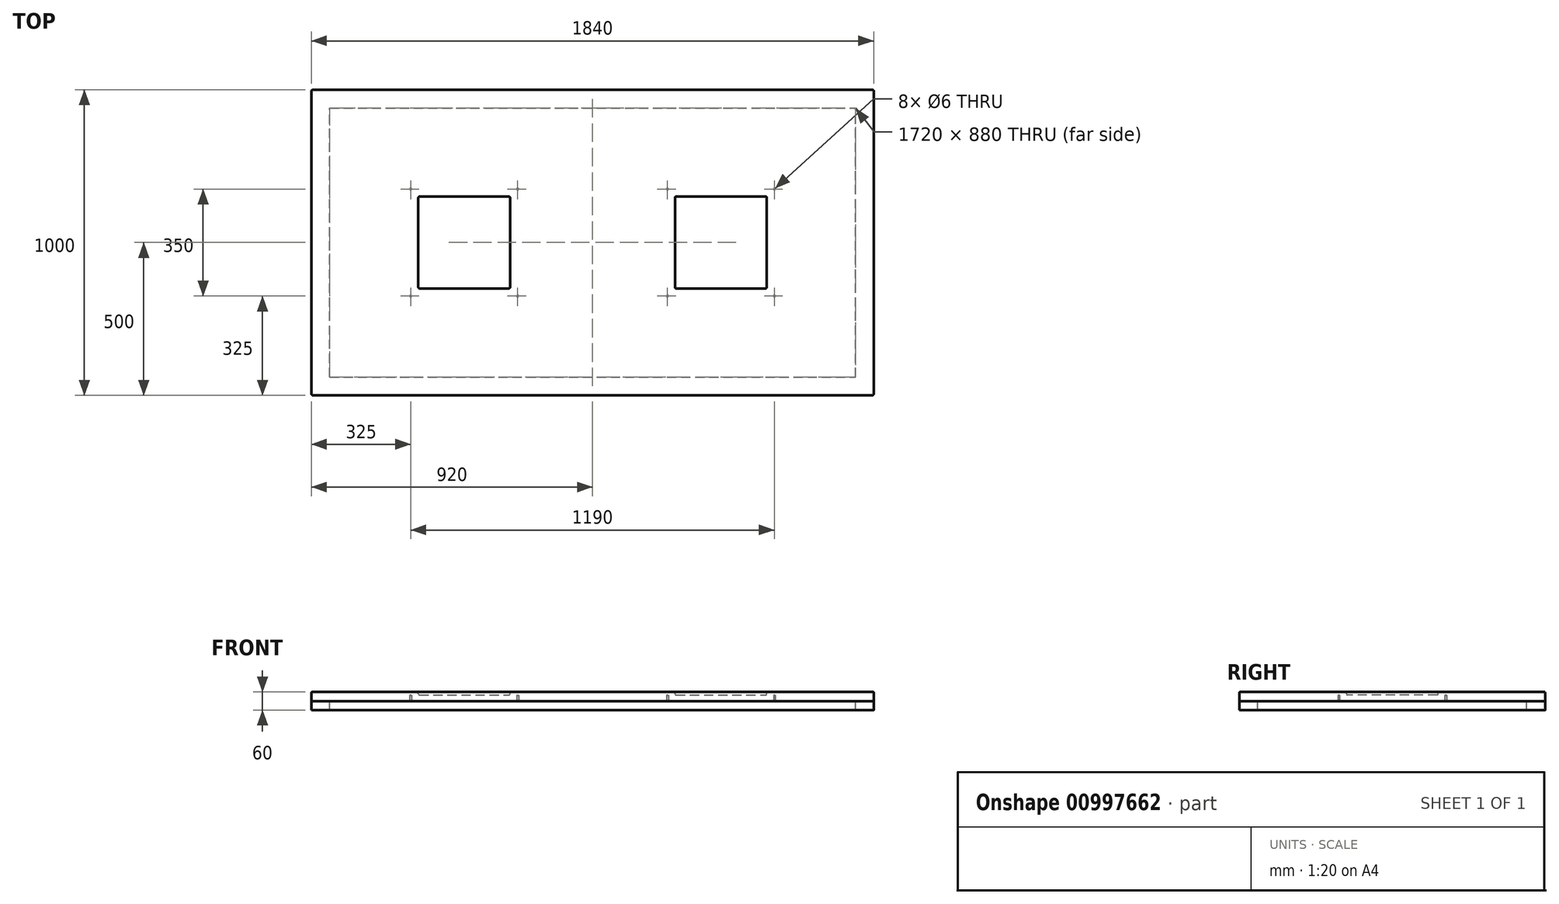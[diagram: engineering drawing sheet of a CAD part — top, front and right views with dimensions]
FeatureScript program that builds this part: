
annotation { "Feature Type Name" : "Feature", "Feature Type Description" : "" }
export const myFeature = defineFeature(function(context is Context, id is Id, definition is map)
    precondition{}
    {
        {
            var Q0;
            Q0=qCreatedBy(makeId("Top.planeOp"),FACE);
            var sketch = newSketch(context, id + "F0", { "sketchPlane" : qUnion([Q0])});
            skLineSegment(sketch, "E0.bottom", {"start": v(0, 0) * mm, "end": v(1840, 0) * mm});
            skLineSegment(sketch, "E0.top", {"start": v(0, 1000) * mm, "end": v(1840, 1000) * mm});
            skLineSegment(sketch, "E0.left", {"start": v(0, 0) * mm, "end": v(0, 1000) * mm});
            skLineSegment(sketch, "E0.right", {"start": v(1840, 0) * mm, "end": v(1840, 1000) * mm});
            skSolve(sketch);
        }
        {
            var Q0;
            Q0=makeQuery(id+"F0.imprint","IMPRINT",FACE,{"disambiguationData":[TD([[makeQuery(id+"F0.imprint","IMPRINT",EDGE,{"derivedFrom":sQuery(id+"F0.wireOp",EDGE,"E0.bottom")}),1.0]])]});
            extrude(context, id + "F1", {"entities" : qUnion([Q0]), "depth" : 30 * mm, "offsetDistance" : 25 * mm});
        }
        {
            var Q0;
            Q0=makeQuery(id+"F1.opExtrude","CAP_FACE",FACE,{"disambiguationData":[OSD([sQuery(id+"F0.wireOp",EDGE,"E0.bottom"),sQuery(id+"F0.wireOp",EDGE,"E0.top"),sQuery(id+"F0.wireOp",EDGE,"E0.left"),sQuery(id+"F0.wireOp",EDGE,"E0.right")])],"isStart":false});
            var sketch = newSketch(context, id + "F2", { "sketchPlane" : qUnion([Q0])});
            skLineSegment(sketch, "E1.bottom", {"start": v(350, 650) * mm, "end": v(650, 650) * mm});
            skLineSegment(sketch, "E1.top", {"start": v(350, 350) * mm, "end": v(650, 350) * mm});
            skLineSegment(sketch, "E1.left", {"start": v(350, 650) * mm, "end": v(350, 350) * mm});
            skLineSegment(sketch, "E1.right", {"start": v(650, 650) * mm, "end": v(650, 350) * mm});
            skLineSegment(sketch, "E2.bottom", {"start": v(1190, 650) * mm, "end": v(1490, 650) * mm});
            skLineSegment(sketch, "E2.top", {"start": v(1190, 350) * mm, "end": v(1490, 350) * mm});
            skLineSegment(sketch, "E2.left", {"start": v(1190, 650) * mm, "end": v(1190, 350) * mm});
            skLineSegment(sketch, "E2.right", {"start": v(1490, 650) * mm, "end": v(1490, 350) * mm});
            skSolve(sketch);
        }
        {
            var Q0;
            Q0=makeQuery(id+"F2.imprint","IMPRINT",FACE,{"disambiguationData":[TD([[makeQuery(id+"F2.imprint","IMPRINT",EDGE,{"derivedFrom":sQuery(id+"F2.wireOp",EDGE,"E2.bottom")}),-1.0]])]});
            var Q1;
            Q1=makeQuery(id+"F2.imprint","IMPRINT",FACE,{"disambiguationData":[TD([[makeQuery(id+"F2.imprint","IMPRINT",EDGE,{"derivedFrom":sQuery(id+"F2.wireOp",EDGE,"E1.bottom")}),-1.0]])]});
            extrude(context, id + "F3", {"entities" : qUnion([Q0, Q1]), "operationType" : NewBodyOperationType.REMOVE, "oppositeDirection" : true, "depth" : 10 * mm, "offsetDistance" : 25 * mm});
        }
        {
            var Q0;
            Q0=makeQuery(id+"F3.boolean.opBoolean","COPY",EDGE,{"derivedFrom":makeQuery(id+"F3.opExtrude","SWEPT_EDGE",EDGE,{"disambiguationData":[OSD([sQuery(id+"F2.wireOp",EDGE,"E2.bottom"),sQuery(id+"F2.wireOp",EDGE,"E2.right")])]})});
            var Q1;
            Q1=makeQuery(id+"F3.boolean.opBoolean","COPY",EDGE,{"derivedFrom":makeQuery(id+"F3.opExtrude","SWEPT_EDGE",EDGE,{"disambiguationData":[OSD([sQuery(id+"F2.wireOp",EDGE,"E2.bottom"),sQuery(id+"F2.wireOp",EDGE,"E2.left")])]})});
            var Q2;
            Q2=makeQuery(id+"F3.boolean.opBoolean","COPY",EDGE,{"derivedFrom":makeQuery(id+"F3.opExtrude","SWEPT_EDGE",EDGE,{"disambiguationData":[OSD([sQuery(id+"F2.wireOp",EDGE,"E2.top"),sQuery(id+"F2.wireOp",EDGE,"E2.left")])]})});
            var Q3;
            Q3=makeQuery(id+"F3.boolean.opBoolean","COPY",EDGE,{"derivedFrom":makeQuery(id+"F3.opExtrude","SWEPT_EDGE",EDGE,{"disambiguationData":[OSD([sQuery(id+"F2.wireOp",EDGE,"E2.top"),sQuery(id+"F2.wireOp",EDGE,"E2.right")])]})});
            var Q4;
            Q4=makeQuery(id+"F3.boolean.opBoolean","COPY",EDGE,{"derivedFrom":makeQuery(id+"F3.opExtrude","SWEPT_EDGE",EDGE,{"disambiguationData":[OSD([sQuery(id+"F2.wireOp",EDGE,"E1.bottom"),sQuery(id+"F2.wireOp",EDGE,"E1.right")])]})});
            var Q5;
            Q5=makeQuery(id+"F3.boolean.opBoolean","COPY",EDGE,{"derivedFrom":makeQuery(id+"F3.opExtrude","SWEPT_EDGE",EDGE,{"disambiguationData":[OSD([sQuery(id+"F2.wireOp",EDGE,"E1.bottom"),sQuery(id+"F2.wireOp",EDGE,"E1.left")])]})});
            var Q6;
            Q6=makeQuery(id+"F3.boolean.opBoolean","COPY",EDGE,{"derivedFrom":makeQuery(id+"F3.opExtrude","SWEPT_EDGE",EDGE,{"disambiguationData":[OSD([sQuery(id+"F2.wireOp",EDGE,"E1.top"),sQuery(id+"F2.wireOp",EDGE,"E1.left")])]})});
            var Q7;
            Q7=makeQuery(id+"F3.boolean.opBoolean","COPY",EDGE,{"derivedFrom":makeQuery(id+"F3.opExtrude","SWEPT_EDGE",EDGE,{"disambiguationData":[OSD([sQuery(id+"F2.wireOp",EDGE,"E1.top"),sQuery(id+"F2.wireOp",EDGE,"E1.right")])]})});
            var Q8;
            Q8=makeQuery(id+"F3.boolean.opBoolean","COPY",FACE,{"derivedFrom":makeQuery(id+"F3.opExtrude","CAP_FACE",FACE,{"disambiguationData":[OSD([sQuery(id+"F2.wireOp",EDGE,"E2.bottom"),sQuery(id+"F2.wireOp",EDGE,"E2.top"),sQuery(id+"F2.wireOp",EDGE,"E2.left"),sQuery(id+"F2.wireOp",EDGE,"E2.right")])],"isStart":false})});
            var Q9;
            Q9=makeQuery(id+"F3.boolean.opBoolean","COPY",EDGE,{"derivedFrom":makeQuery(id+"F3.opExtrude","CAP_EDGE",EDGE,{"disambiguationData":[OSD([sQuery(id+"F2.wireOp",EDGE,"E1.right")])],"isStart":false})});
            var Q10;
            Q10=makeQuery(id+"F3.boolean.opBoolean","COPY",EDGE,{"derivedFrom":makeQuery(id+"F3.opExtrude","CAP_EDGE",EDGE,{"disambiguationData":[OSD([sQuery(id+"F2.wireOp",EDGE,"E1.bottom")])],"isStart":false})});
            var Q11;
            Q11=makeQuery(id+"F3.boolean.opBoolean","COPY",EDGE,{"derivedFrom":makeQuery(id+"F3.opExtrude","CAP_EDGE",EDGE,{"disambiguationData":[OSD([sQuery(id+"F2.wireOp",EDGE,"E1.left")])],"isStart":false})});
            var Q12;
            Q12=makeQuery(id+"F3.boolean.opBoolean","COPY",EDGE,{"derivedFrom":makeQuery(id+"F3.opExtrude","CAP_EDGE",EDGE,{"disambiguationData":[OSD([sQuery(id+"F2.wireOp",EDGE,"E1.top")])],"isStart":false})});
            var Q13;
            Q13=makeQuery(id+"F1.opExtrude","CAP_EDGE",EDGE,{"disambiguationData":[OSD([sQuery(id+"F0.wireOp",EDGE,"E0.left")])],"isStart":false});
            var Q14;
            Q14=makeQuery(id+"F1.opExtrude","CAP_EDGE",EDGE,{"disambiguationData":[OSD([sQuery(id+"F0.wireOp",EDGE,"E0.bottom")])],"isStart":false});
            var Q15;
            Q15=makeQuery(id+"F1.opExtrude","CAP_EDGE",EDGE,{"disambiguationData":[OSD([sQuery(id+"F0.wireOp",EDGE,"E0.right")])],"isStart":false});
            var Q16;
            Q16=makeQuery(id+"F1.opExtrude","CAP_EDGE",EDGE,{"disambiguationData":[OSD([sQuery(id+"F0.wireOp",EDGE,"E0.top")])],"isStart":false});
            fillet(context, id + "F4", {"entities" : qUnion([Q0, Q1, Q2, Q3, Q4, Q5, Q6, Q7, Q8, Q9, Q10, Q11, Q12, Q13, Q14, Q15, Q16]), "tangentPropagation" : true, "radius" : 3 * mm, "defaultsChanged" : false, "vertexSettings" : [], "allowEdgeOverflow" : false});
        }
        {
            var Q0;
            Q0=makeQuery(id+"F1.opExtrude","SWEPT_EDGE",EDGE,{"disambiguationData":[OSD([sQuery(id+"F0.wireOp",EDGE,"E0.top"),sQuery(id+"F0.wireOp",EDGE,"E0.right")])]});
            var Q1;
            Q1=makeQuery(id+"F1.opExtrude","SWEPT_EDGE",EDGE,{"disambiguationData":[OSD([sQuery(id+"F0.wireOp",EDGE,"E0.bottom"),sQuery(id+"F0.wireOp",EDGE,"E0.right")])]});
            var Q2;
            Q2=makeQuery(id+"F1.opExtrude","SWEPT_EDGE",EDGE,{"disambiguationData":[OSD([sQuery(id+"F0.wireOp",EDGE,"E0.bottom"),sQuery(id+"F0.wireOp",EDGE,"E0.left")])]});
            var Q3;
            Q3=makeQuery(id+"F1.opExtrude","SWEPT_EDGE",EDGE,{"disambiguationData":[OSD([sQuery(id+"F0.wireOp",EDGE,"E0.top"),sQuery(id+"F0.wireOp",EDGE,"E0.left")])]});
            fillet(context, id + "F5", {"entities" : qUnion([Q0, Q1, Q2, Q3]), "tangentPropagation" : true, "radius" : 5 * mm, "defaultsChanged" : false, "vertexSettings" : [], "allowEdgeOverflow" : false});
        }
        {
            var Q0;
            Q0=makeQuery(id+"F1.opExtrude","CAP_FACE",FACE,{"disambiguationData":[OSD([sQuery(id+"F0.wireOp",EDGE,"E0.bottom"),sQuery(id+"F0.wireOp",EDGE,"E0.top"),sQuery(id+"F0.wireOp",EDGE,"E0.left"),sQuery(id+"F0.wireOp",EDGE,"E0.right")])],"isStart":true});
            var sketch = newSketch(context, id + "F6", { "sketchPlane" : qUnion([Q0])});
            skLineSegment(sketch, "E3.bottom", {"start": v(325, -325) * mm, "end": v(675, -325) * mm, "construction": true});
            skLineSegment(sketch, "E3.top", {"start": v(325, -675) * mm, "end": v(675, -675) * mm, "construction": true});
            skLineSegment(sketch, "E3.left", {"start": v(325, -325) * mm, "end": v(325, -675) * mm, "construction": true});
            skLineSegment(sketch, "E3.right", {"start": v(675, -325) * mm, "end": v(675, -675) * mm, "construction": true});
            skLineSegment(sketch, "E4.bottom", {"start": v(400, -400) * mm, "end": v(600, -400) * mm, "construction": true});
            skLineSegment(sketch, "E4.top", {"start": v(400, -600) * mm, "end": v(600, -600) * mm, "construction": true});
            skLineSegment(sketch, "E4.left", {"start": v(400, -400) * mm, "end": v(400, -600) * mm, "construction": true});
            skLineSegment(sketch, "E4.right", {"start": v(600, -400) * mm, "end": v(600, -600) * mm, "construction": true});
            skLineSegment(sketch, "E5.1.0.0", {"start": v(1165, -325) * mm, "end": v(1515, -325) * mm, "construction": true});
            skLineSegment(sketch, "E5.1.0.1", {"start": v(1165, -325) * mm, "end": v(1165, -675) * mm, "construction": true});
            skLineSegment(sketch, "E5.1.0.2", {"start": v(1240, -400) * mm, "end": v(1240, -600) * mm, "construction": true});
            skLineSegment(sketch, "E5.1.0.3", {"start": v(1240, -400) * mm, "end": v(1440, -400) * mm, "construction": true});
            skLineSegment(sketch, "E5.1.0.4", {"start": v(1440, -400) * mm, "end": v(1440, -600) * mm, "construction": true});
            skLineSegment(sketch, "E5.1.0.5", {"start": v(1240, -600) * mm, "end": v(1440, -600) * mm, "construction": true});
            skLineSegment(sketch, "E5.1.0.6", {"start": v(1515, -325) * mm, "end": v(1515, -675) * mm, "construction": true});
            skLineSegment(sketch, "E5.1.0.7", {"start": v(1165, -675) * mm, "end": v(1515, -675) * mm, "construction": true});
            skLineSegment(sketch, "E5.direction1", {"start": v(325, -675) * mm, "end": v(1165, -675) * mm, "construction": true});
            skSolve(sketch);
        }
        {
            var Q0;
            Q0=sQuery(id+"F6.wireOp",VERTEX,"E3.bottom.start");
            var Q1;
            Q1=sQuery(id+"F6.wireOp",VERTEX,"E3.bottom.end");
            var Q2;
            Q2=sQuery(id+"F6.wireOp",VERTEX,"E3.top.start");
            var Q3;
            Q3=sQuery(id+"F6.wireOp",VERTEX,"E3.top.end");
            var Q4;
            Q4=sQuery(id+"F6.wireOp",VERTEX,"E5.1.0.1.end");
            var Q5;
            Q5=sQuery(id+"F6.wireOp",VERTEX,"E5.1.0.0.start");
            var Q6;
            Q6=sQuery(id+"F6.wireOp",VERTEX,"E5.1.0.0.end");
            var Q7;
            Q7=sQuery(id+"F6.wireOp",VERTEX,"E5.1.0.6.end");
            var Q8;
            Q8=makeQuery(id+"F1.opExtrude","SWEPT_BODY",BODY,{"disambiguationData":[OSD([sQuery(id+"F0.wireOp",EDGE,"E0.bottom"),sQuery(id+"F0.wireOp",EDGE,"E0.top"),sQuery(id+"F0.wireOp",EDGE,"E0.left"),sQuery(id+"F0.wireOp",EDGE,"E0.right")])]});
            hole(context, id + "F7", {"style" : HoleStyle.SIMPLE, "endStyle" : HoleEndStyle.BLIND, "holeDiameter" : 6 * mm, "majorDiameter" : 5 * mm, "holeDepth" : 18 * mm, "isTappedThrough" : true, "tappedDepth" : 12 * mm, "tapClearance" : 3, "locations" : qUnion([Q0, Q1, Q2, Q3, Q4, Q5, Q6, Q7]), "scope" : qUnion([Q8])});
        }
        {
            var Q0;
            Q0=makeQuery(id+"F1.opExtrude","CAP_FACE",FACE,{"disambiguationData":[OSD([sQuery(id+"F0.wireOp",EDGE,"E0.bottom"),sQuery(id+"F0.wireOp",EDGE,"E0.top"),sQuery(id+"F0.wireOp",EDGE,"E0.left"),sQuery(id+"F0.wireOp",EDGE,"E0.right")])],"isStart":true});
            var sketch = newSketch(context, id + "F8", { "sketchPlane" : qUnion([Q0])});
            skLineSegment(sketch, "E6.bottom", {"start": v(0, 0) * mm, "end": v(1840, 0) * mm});
            skLineSegment(sketch, "E6.top", {"start": v(0, -1000) * mm, "end": v(1840, -1000) * mm});
            skLineSegment(sketch, "E6.left", {"start": v(0, 0) * mm, "end": v(0, -1000) * mm});
            skLineSegment(sketch, "E6.right", {"start": v(1840, 0) * mm, "end": v(1840, -1000) * mm});
            skLineSegment(sketch, "E7.bottom", {"start": v(60, -60) * mm, "end": v(1780, -60) * mm});
            skLineSegment(sketch, "E7.top", {"start": v(60, -940) * mm, "end": v(1780, -940) * mm});
            skLineSegment(sketch, "E7.left", {"start": v(60, -60) * mm, "end": v(60, -940) * mm});
            skLineSegment(sketch, "E7.right", {"start": v(1780, -60) * mm, "end": v(1780, -940) * mm});
            skSolve(sketch);
        }
        {
            var Q0;
            Q0=makeQuery(id+"F8.imprint","IMPRINT",FACE,{"disambiguationData":[TD([[makeQuery(id+"F8.imprint","IMPRINT",EDGE,{"derivedFrom":sQuery(id+"F8.wireOp",EDGE,"E7.bottom")}),1.0]])]});
            extrude(context, id + "F9", {"entities" : qUnion([Q0]), "depth" : 30 * mm, "offsetDistance" : 25 * mm});
        }
    });
